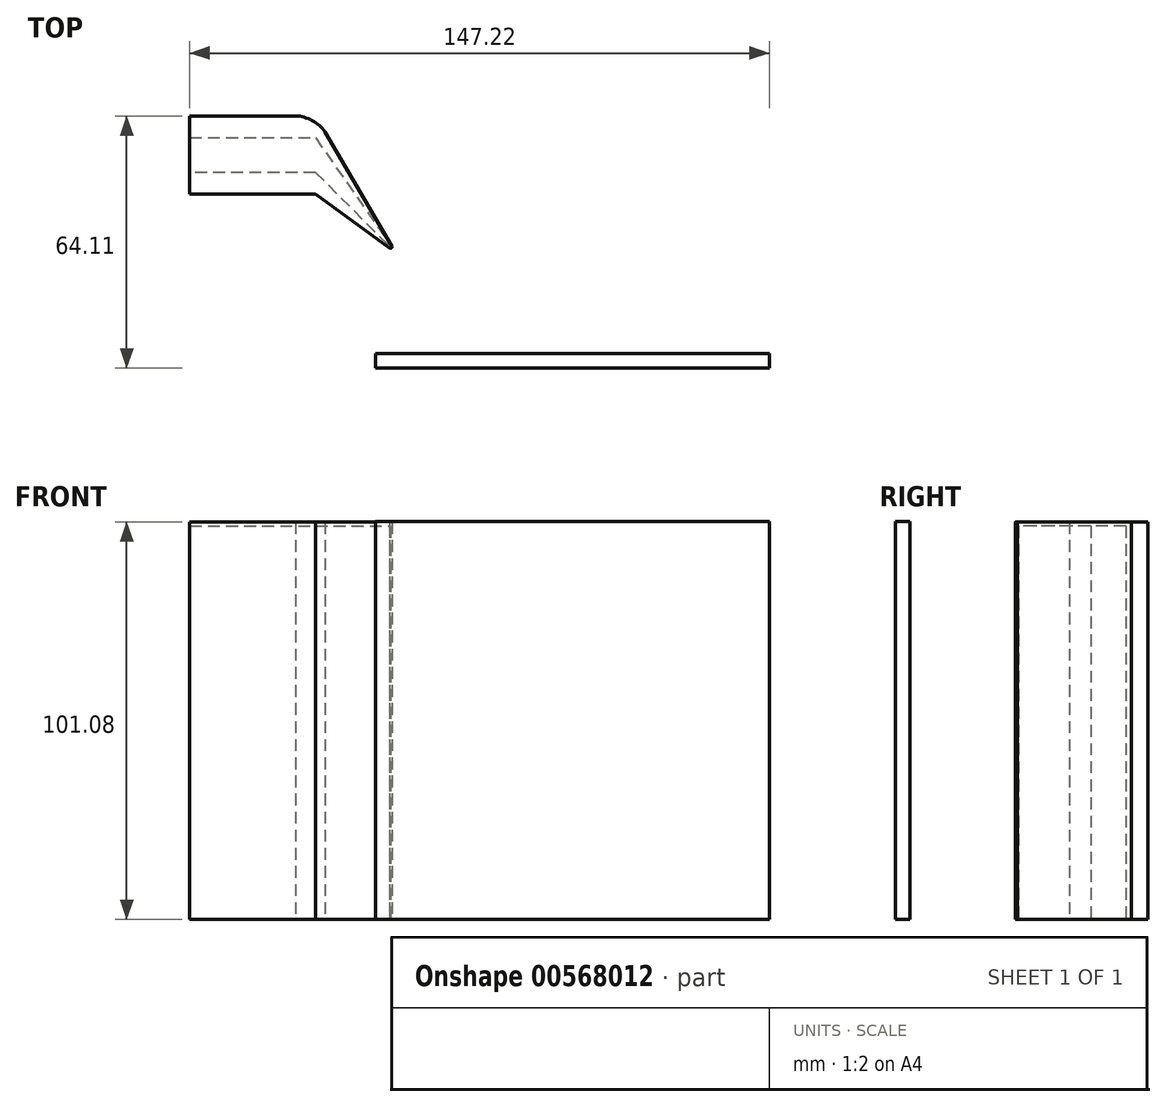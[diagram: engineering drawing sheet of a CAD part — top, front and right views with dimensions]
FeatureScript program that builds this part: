
annotation { "Feature Type Name" : "Feature", "Feature Type Description" : "" }
export const myFeature = defineFeature(function(context is Context, id is Id, definition is map)
    precondition{}
    {
        {
            var Q0;
            Q0=qCreatedBy(makeId("Top.planeOp"),FACE);
            var sketch = newSketch(context, id + "F0", { "sketchPlane" : qUnion([Q0])});
            skLineSegment(sketch, "E0", {"start": v(-47.22, 46.06) * mm, "end": v(-47.22, 40.5) * mm});
            skLineSegment(sketch, "E1", {"start": v(-47.22, 40.5) * mm, "end": v(-15.28, 40.5) * mm});
            skLineSegment(sketch, "E2", {"start": v(-15.28, 40.5) * mm, "end": v(3.51, 26.84) * mm});
            skLineSegment(sketch, "E3", {"start": v(4.17, 27.27) * mm, "end": v(-12.83, 56.24) * mm});
            skLineSegment(sketch, "E4", {"start": v(-20.38, 60.41) * mm, "end": v(-47.22, 60.41) * mm});
            skLineSegment(sketch, "E5", {"start": v(-47.22, 60.41) * mm, "end": v(-47.22, 54.86) * mm});
            skLineSegment(sketch, "E6", {"start": v(-47.22, 54.86) * mm, "end": v(-15.28, 54.86) * mm});
            skLineSegment(sketch, "E7", {"start": v(-15.28, 54.86) * mm, "end": v(3.76, 27.6) * mm});
            skLineSegment(sketch, "E8", {"start": v(-15.28, 46.06) * mm, "end": v(-47.22, 46.06) * mm});
            skLineSegment(sketch, "E9", {"start": v(-15.28, 46.06) * mm, "end": v(3.51, 27.27) * mm});
            skLineSegment(sketch, "E10", {"start": v(3.76, 27.6) * mm, "end": v(3.51, 27.27) * mm});
            skArc(sketch, "E11", {"start": v(-12.83, 56.24) * mm, "mid": v(-16.11, 59.22) * mm, "end": v(-20.38, 60.41) * mm});
            skArc(sketch, "E12", {"start": v(3.51, 26.84) * mm, "mid": v(3.99, 26.84) * mm, "end": v(4.17, 27.27) * mm});
            skPoint(sketch, "E13.orphan", {"position": v(-15.28, 60.41) * mm});
            skSolve(sketch);
        }
        {
            var Q0;
            Q0=makeQuery(id+"F0.imprint","IMPRINT",FACE,{"disambiguationData":[TD([[makeQuery(id+"F0.imprint","IMPRINT",EDGE,{"derivedFrom":sQuery(id+"F0.wireOp",EDGE,"E0")}),1.0]])]});
            extrude(context, id + "F1", {"entities" : qUnion([Q0]), "depth" : 100 * mm, "offsetDistance" : 25 * mm});
        }
        {
            var Q0;
            Q0=makeQuery(id+"F1.opExtrude","CAP_FACE",FACE,{"disambiguationData":[OSD([sQuery(id+"F0.wireOp",EDGE,"E0"),sQuery(id+"F0.wireOp",EDGE,"E1"),sQuery(id+"F0.wireOp",EDGE,"E2"),sQuery(id+"F0.wireOp",EDGE,"E3"),sQuery(id+"F0.wireOp",EDGE,"E4"),sQuery(id+"F0.wireOp",EDGE,"E5"),sQuery(id+"F0.wireOp",EDGE,"E6"),sQuery(id+"F0.wireOp",EDGE,"E7"),sQuery(id+"F0.wireOp",EDGE,"E8"),sQuery(id+"F0.wireOp",EDGE,"E9"),sQuery(id+"F0.wireOp",EDGE,"E10"),sQuery(id+"F0.wireOp",EDGE,"E11"),sQuery(id+"F0.wireOp",EDGE,"E12")])],"isStart":false});
            var sketch = newSketch(context, id + "F2", { "sketchPlane" : qUnion([Q0])});
            skLineSegment(sketch, "E14", {"start": v(-47.22, 60.41) * mm, "end": v(-47.22, 40.5) * mm});
            skLineSegment(sketch, "E15", {"start": v(-47.22, 40.5) * mm, "end": v(-15.28, 40.5) * mm});
            skLineSegment(sketch, "E16", {"start": v(-15.28, 40.5) * mm, "end": v(3.51, 26.84) * mm});
            skLineSegment(sketch, "E17", {"start": v(-47.22, 60.41) * mm, "end": v(-20.38, 60.41) * mm});
            skLineSegment(sketch, "E18", {"start": v(4.17, 27.27) * mm, "end": v(-12.83, 56.24) * mm});
            skArc(sketch, "E19", {"start": v(3.51, 26.84) * mm, "mid": v(3.99, 26.83) * mm, "end": v(4.17, 27.27) * mm});
            skArc(sketch, "E20", {"start": v(-12.83, 56.24) * mm, "mid": v(-16.07, 59.3) * mm, "end": v(-20.38, 60.41) * mm});
            skSolve(sketch);
        }
        {
            var Q0;
            {var subQ2=makeQuery(id+"F1.opExtrude","CAP_EDGE",EDGE,{"disambiguationData":[OSD([sQuery(id+"F0.wireOp",EDGE,"E6")])],"isStart":false});Q0=makeQuery(id+"F2.imprint","IMPRINT",FACE,{"disambiguationData":[TD([[makeQuery(id+"F2.imprint","IMPRINT",EDGE,{"derivedFrom":subQ2}),-1.0]])]});}
            var Q1;
            {var subQ4=sQuery(id+"F2.wireOp",EDGE,"E15");Q1=makeQuery(id+"F2.imprint","IMPRINT",FACE,{"disambiguationData":[TD([[makeQuery(id+"F2.imprint","IMPRINT",EDGE,{"derivedFrom":subQ4}),1.0]])]});}
            extrude(context, id + "F3", {"entities" : qUnion([Q0, Q1]), "operationType" : NewBodyOperationType.ADD, "depth" : 1 * mm, "offsetDistance" : 25 * mm});
        }
        {
            var Q0;
            Q0=qCreatedBy(makeId("Right.planeOp"),FACE);
            var sketch = newSketch(context, id + "F4", { "sketchPlane" : qUnion([Q0])});
            skLineSegment(sketch, "E21", {"start": v(0, 0) * mm, "end": v(0, 101.08) * mm});
            skLineSegment(sketch, "E22", {"start": v(0, 101.08) * mm, "end": v(-3.7, 101.08) * mm});
            skLineSegment(sketch, "E23", {"start": v(-3.7, 101.08) * mm, "end": v(-3.7, 0) * mm});
            skLineSegment(sketch, "E24", {"start": v(-3.7, 0) * mm, "end": v(0, 0) * mm});
            skSolve(sketch);
        }
        {
            var Q0;
            Q0=makeQuery(id+"F4.imprint","IMPRINT",FACE,{"disambiguationData":[TD([[makeQuery(id+"F4.imprint","IMPRINT",EDGE,{"derivedFrom":sQuery(id+"F4.wireOp",EDGE,"E21")}),1.0]])]});
            extrude(context, id + "F5", {"entities" : qUnion([Q0]), "depth" : 100 * mm, "offsetDistance" : 25 * mm});
        }
    });
